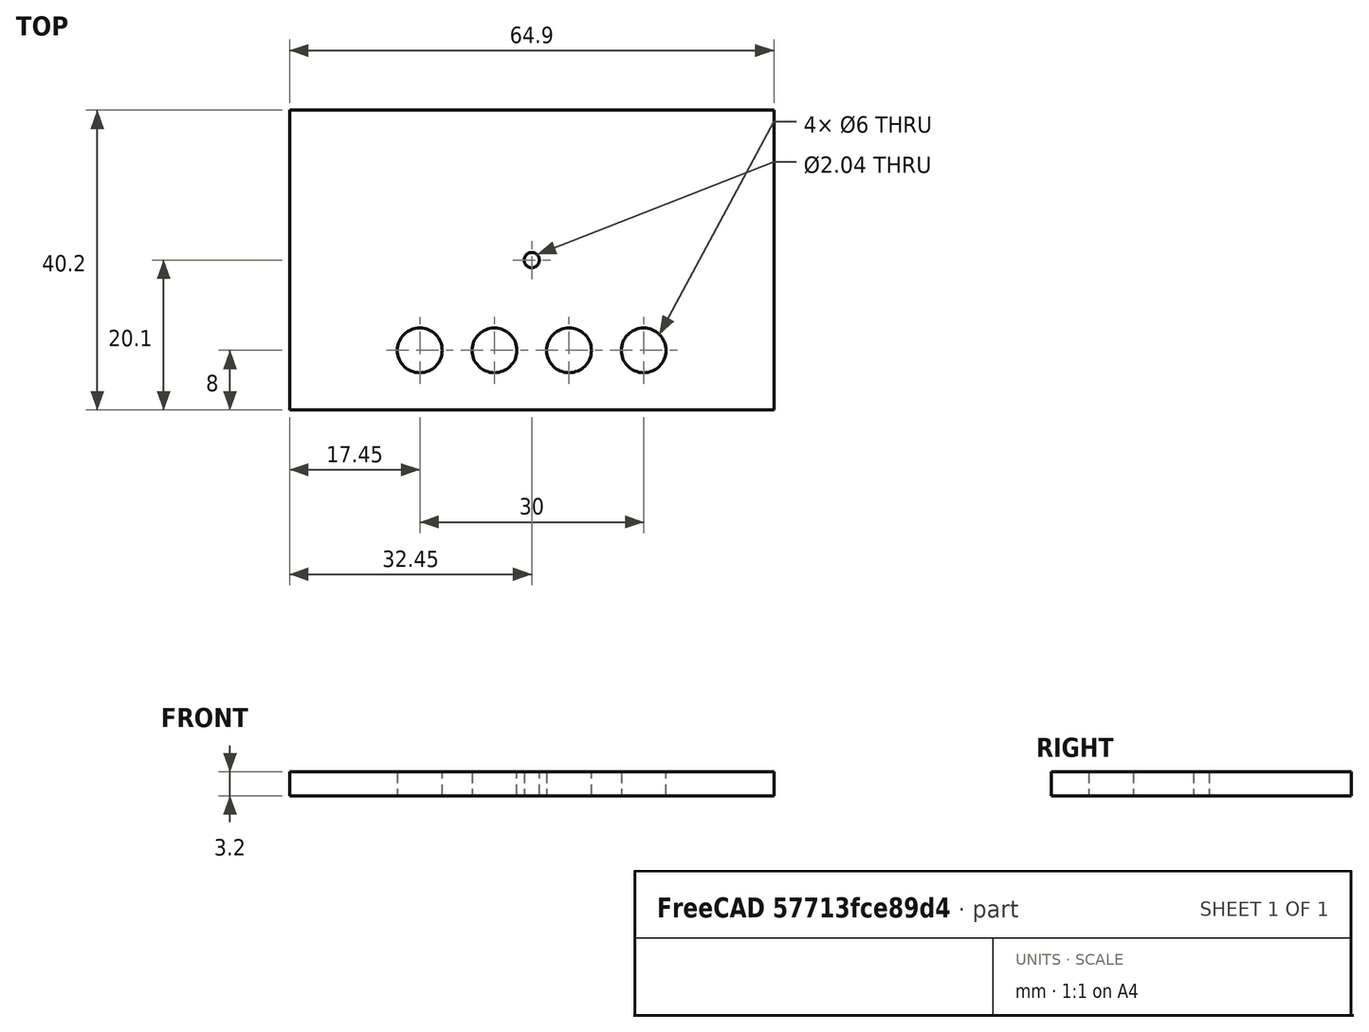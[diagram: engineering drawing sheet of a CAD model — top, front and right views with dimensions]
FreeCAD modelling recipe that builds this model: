
FCSTD DOCUMENT  (FreeCAD 0.21R33694 (Git))
Label: leftside-fc21-1
License: All rights reserved
LicenseURL: http://en.wikipedia.org/wiki/All_rights_reserved
objects: Sketcher::SketchObject×1, PartDesign::Pad×1, PartDesign::Body×1
note: 4 computed .brp shape members not serialized (recipe doc carries the construction recipe); baked Part::Feature solids carry a one-line shape summary decoded from their .brp

FEATURE [Sketcher::SketchObject] Sketch
  FullyConstrained = true
  MapMode = 5
  Support = -> [XY_Plane]
  sketch-geometry (12):
    g0: LineSegment StartX=-32.45 StartY=20.1 StartZ=0 EndX=32.45 EndY=20.1 EndZ=0
    g1: LineSegment StartX=32.45 StartY=20.1 StartZ=0 EndX=32.45 EndY=-20.1 EndZ=0
    g2: LineSegment StartX=32.45 StartY=-20.1 StartZ=0 EndX=-32.45 EndY=-20.1 EndZ=0
    g3: LineSegment StartX=-32.45 StartY=-20.1 StartZ=0 EndX=-32.45 EndY=20.1 EndZ=0
    g4: Circle CenterX=0 CenterY=0 CenterZ=0 NormalX=0 NormalY=0 NormalZ=1 AngleXU=0 Radius=1.02
    g5: Circle CenterX=15 CenterY=-12.1 CenterZ=0 NormalX=0 NormalY=0 NormalZ=1 AngleXU=0 Radius=3
    g6: Circle CenterX=5 CenterY=-12.1 CenterZ=0 NormalX=0 NormalY=0 NormalZ=1 AngleXU=0 Radius=3
    g7: Circle CenterX=-5 CenterY=-12.1 CenterZ=0 NormalX=0 NormalY=0 NormalZ=1 AngleXU=0 Radius=3
    g8: LineSegment StartX=15 StartY=-12.1 StartZ=0 EndX=5 EndY=-12.1 EndZ=0
    g9: LineSegment StartX=5 StartY=-12.1 StartZ=0 EndX=-5 EndY=-12.1 EndZ=0
    g10: Circle CenterX=-15 CenterY=-12.1 CenterZ=0 NormalX=0 NormalY=0 NormalZ=1 AngleXU=0 Radius=3
    g11: LineSegment StartX=-5 StartY=-12.1 StartZ=0 EndX=-15 EndY=-12.1 EndZ=0
  constraints (29):
    c: Coincident(g0,g1)
    c: Coincident(g1,g2)
    c: Coincident(g2,g3)
    c: Coincident(g3,g0)
    c: Horizontal(g0)
    c: Vertical(g3)
    c: DistanceY(g1,g0) = 40.2
    c: Symmetric(g1,g0,g-1)
    c: Symmetric(g2,g1,g-2)
    c: Coincident(g4,g-1)
    c: Radius(g4) = 1.02
    c: DistanceX(g2,g1) = 64.9
    c: Equal(g7,g6)
    c: Equal(g6,g5)
    c: Coincident(g8,g5)
    c: Coincident(g8,g6)
    c: Horizontal(g8)
    c: Coincident(g9,g6)
    c: Coincident(g9,g7)
    c: Equal(g8,g9)
    c: Radius(g5) = 3
    c: Equal(g10,g7)
    c: Coincident(g11,g7)
    c: Coincident(g11,g10)
    c: Horizontal(g11)
    c: Equal(g11,g9)
    c: DistanceX(g11,g11) = 10
    c: Symmetric(g6,g7,g-2)
    c: DistanceY(g2,g10) = 8
FEATURE [PartDesign::Pad] Pad
  Direction = (0,0,1)
  Length = 3.2
  Length2 = 10
  Profile = -> Sketch
  ReferenceAxis = -> Sketch [N_Axis]
  Type = 0
FEATURE [PartDesign::Body] Body
  Group = -> [Sketch,Pad]
  Origin = -> Origin
  Tip = -> Pad
